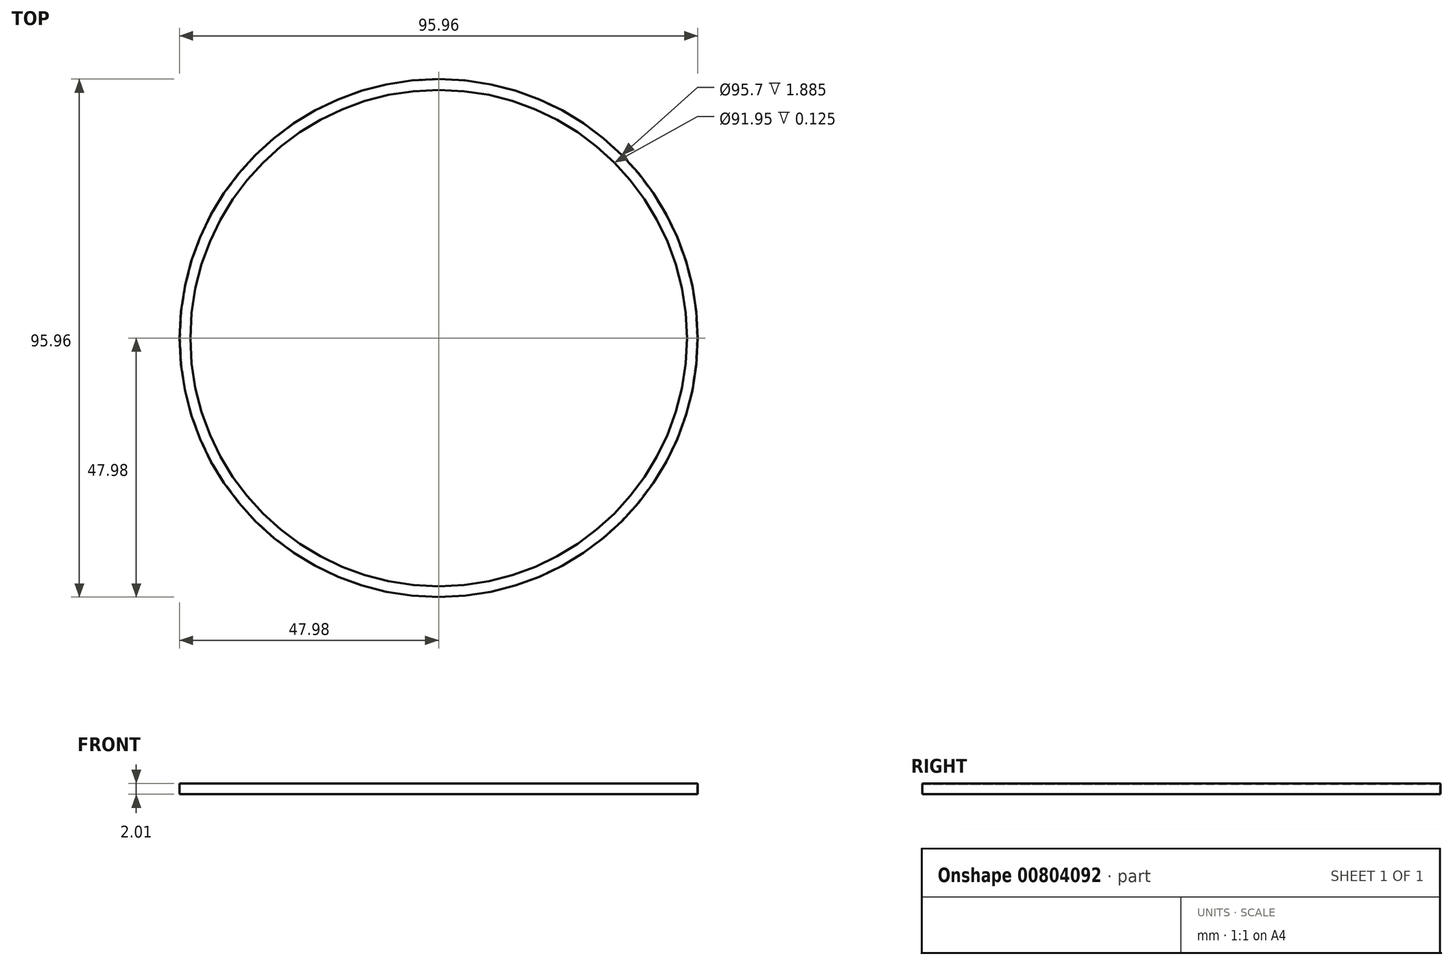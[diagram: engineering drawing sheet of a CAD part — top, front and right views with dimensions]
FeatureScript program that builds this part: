
annotation { "Feature Type Name" : "Feature", "Feature Type Description" : "" }
export const myFeature = defineFeature(function(context is Context, id is Id, definition is map)
    precondition{}
    {
        {
            var Q0;
            Q0=qCreatedBy(makeId("Front.planeOp"),FACE);
            var sketch = newSketch(context, id + "F0", { "sketchPlane" : qUnion([Q0])});
            skLineSegment(sketch, "E0", {"start": v(0, 0) * mm, "end": v(0, -6.48) * mm});
            skSolve(sketch);
        }
        {
            var Q0;
            Q0=qCreatedBy(makeId("Front.planeOp"),FACE);
            var sketch = newSketch(context, id + "F1", { "sketchPlane" : qUnion([Q0])});
            skLineSegment(sketch, "E1", {"start": v(-47.98, 0) * mm, "end": v(-45.98, 0) * mm});
            skLineSegment(sketch, "E2", {"start": v(-45.98, 0) * mm, "end": v(-45.98, -0.12) * mm});
            skLineSegment(sketch, "E3", {"start": v(-47.98, 0) * mm, "end": v(-47.98, -2) * mm});
            skLineSegment(sketch, "E4", {"start": v(-47.98, -2) * mm, "end": v(-47.85, -2) * mm});
            skLineSegment(sketch, "E5", {"start": v(-47.85, -2) * mm, "end": v(-47.85, -0.12) * mm});
            skLineSegment(sketch, "E6", {"start": v(-47.85, -0.12) * mm, "end": v(-45.98, -0.12) * mm});
            skSolve(sketch);
        }
        {
            var Q0;
            Q0=makeQuery(id+"F1.imprint","IMPRINT",FACE,{"disambiguationData":[TD([[makeQuery(id+"F1.imprint","IMPRINT",EDGE,{"derivedFrom":sQuery(id+"F1.wireOp",EDGE,"E1")}),-1.0]])]});
            var Q1;
            Q1=sQuery(id+"F0.wireOp",EDGE,"E0");
            revolve(context, id + "F2", {"surfaceOperationType" : NewSurfaceOperationType.NEW, "entities" : qUnion([Q0]), "axis" : qUnion([Q1]), "revolveType" : RevolveType.FULL});
        }
    });
